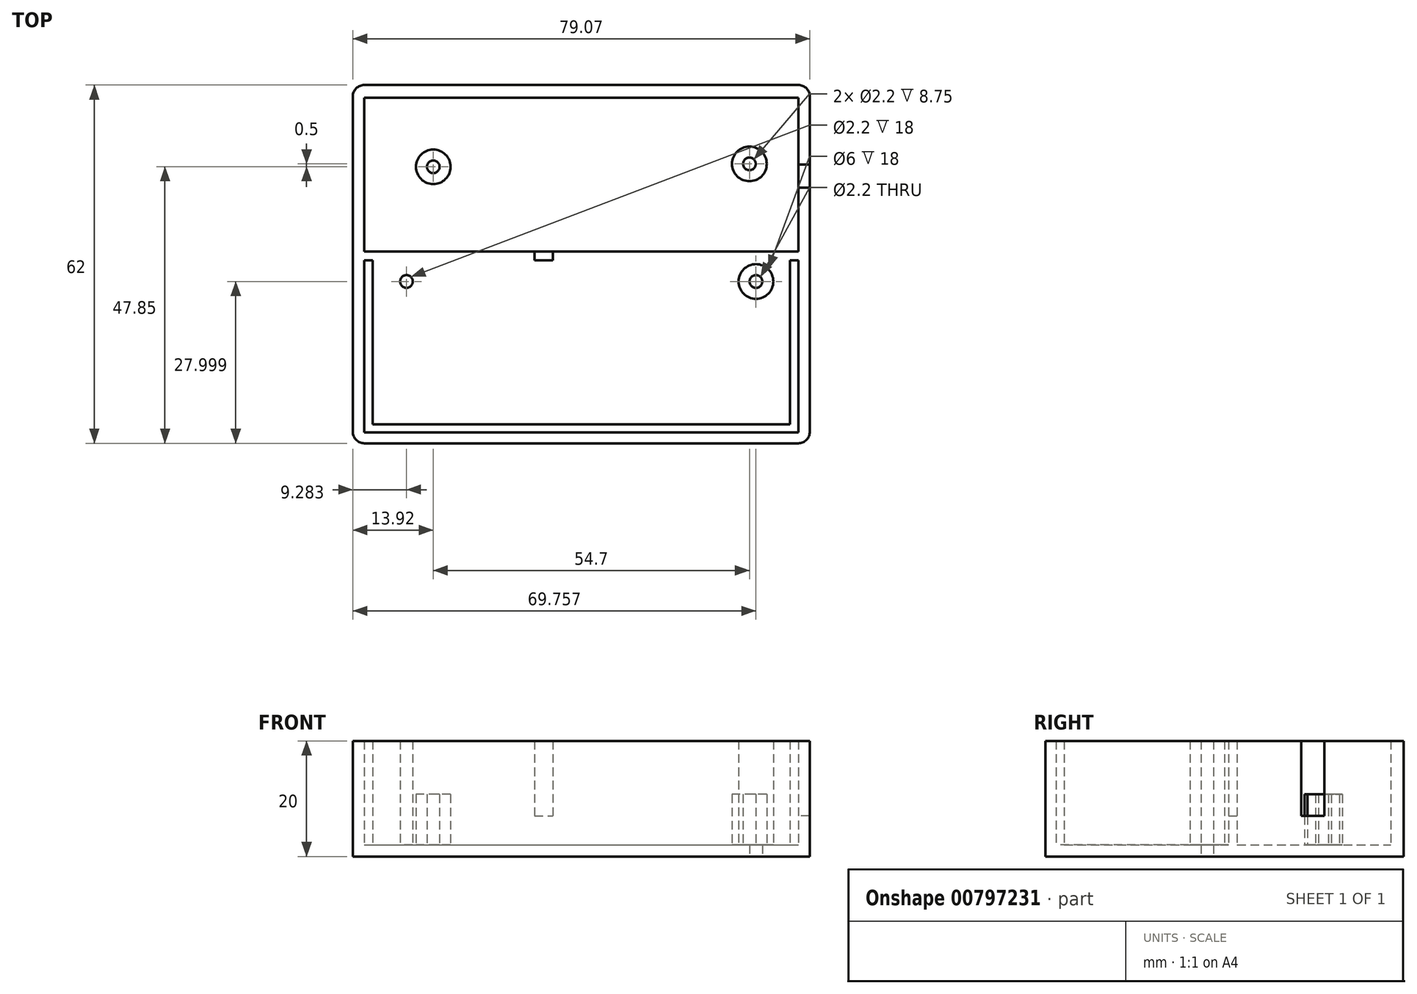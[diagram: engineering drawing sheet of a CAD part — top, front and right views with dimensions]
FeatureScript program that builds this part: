
annotation { "Feature Type Name" : "Feature", "Feature Type Description" : "" }
export const myFeature = defineFeature(function(context is Context, id is Id, definition is map)
    precondition{}
    {
        {
            var Q0;
            Q0=qCreatedBy(makeId("Top.planeOp"),FACE);
            var sketch = newSketch(context, id + "F0", { "sketchPlane" : qUnion([Q0])});
            skPoint(sketch, "E0.middle", {"position": v(0, 0) * mm});
            skLineSegment(sketch, "E1.bottom", {"start": v(36.1, -12.1) * mm, "end": v(-36.1, -12.1) * mm});
            skLineSegment(sketch, "E1.top", {"start": v(36.1, 12.1) * mm, "end": v(-36.1, 12.1) * mm});
            skLineSegment(sketch, "E1.left", {"start": v(36.1, -12.1) * mm, "end": v(36.1, 12.1) * mm});
            skLineSegment(sketch, "E1.right", {"start": v(-36.1, -12.1) * mm, "end": v(-36.1, 12.1) * mm});
            skLineSegment(sketch, "E2", {"start": v(-36.1, 12.1) * mm, "end": v(-25.6, 12.1) * mm});
            skLineSegment(sketch, "E3", {"start": v(-25.6, 12.1) * mm, "end": v(-25.6, 1.6) * mm});
            skLineSegment(sketch, "E4", {"start": v(36.1, 12.1) * mm, "end": v(29.1, 12.1) * mm});
            skLineSegment(sketch, "E5", {"start": v(29.1, 12.1) * mm, "end": v(29.1, 2.1) * mm});
            skLineSegment(sketch, "E6", {"start": v(-37.55, -12.1) * mm, "end": v(-37.55, 13.53) * mm});
            skLineSegment(sketch, "E7", {"start": v(37.55, -2) * mm, "end": v(37.55, 13.53) * mm});
            skLineSegment(sketch, "E8.bottom", {"start": v(-39.55, 15.75) * mm, "end": v(39.55, 15.75) * mm});
            skCircle(sketch, "E9", {"center": v(-25.6, 1.6) * mm, "radius": 3 * mm});
            skCircle(sketch, "E10", {"center": v(29.1, 2.1) * mm, "radius": 3 * mm});
            skCircle(sketch, "E11", {"center": v(-25.6, 1.6) * mm, "radius": 1.1 * mm});
            skCircle(sketch, "E12", {"center": v(29.1, 2.1) * mm, "radius": 1.1 * mm});
            skLineSegment(sketch, "E13", {"start": v(-25.6, 1.6) * mm, "end": v(-22.6, 1.6) * mm});
            skLineSegment(sketch, "E14", {"start": v(39.55, 0) * mm, "end": v(39.55, -2) * mm});
            skLineSegment(sketch, "E15", {"start": v(39.55, 0) * mm, "end": v(39.55, 2) * mm});
            skLineSegment(sketch, "E16", {"start": v(39.55, 2) * mm, "end": v(37.55, 2) * mm});
            skLineSegment(sketch, "E17", {"start": v(39.55, -2) * mm, "end": v(37.55, -2) * mm});
            skLineSegment(sketch, "E18", {"start": v(-36.1, -14.56) * mm, "end": v(36.1, -14.56) * mm});
            skLineSegment(sketch, "E19", {"start": v(-37.55, 13.53) * mm, "end": v(37.55, 13.53) * mm});
            skLineSegment(sketch, "E20", {"start": v(36.1, -43) * mm, "end": v(36.1, -14.56) * mm});
            skLineSegment(sketch, "E21.bottom", {"start": v(39.55, 15.75) * mm, "end": v(-39.52, 15.75) * mm});
            skLineSegment(sketch, "E21.left", {"start": v(39.55, 15.75) * mm, "end": v(39.55, -46.25) * mm});
            skLineSegment(sketch, "E21.right", {"start": v(-39.52, 15.75) * mm, "end": v(-39.52, -46.25) * mm});
            skLineSegment(sketch, "E22.top", {"start": v(-37.55, -44.4) * mm, "end": v(37.55, -44.4) * mm});
            skLineSegment(sketch, "E22.left", {"start": v(-37.55, 13.53) * mm, "end": v(-37.55, -12.1) * mm});
            skLineSegment(sketch, "E22.right", {"start": v(37.55, 13.53) * mm, "end": v(37.55, -2) * mm});
            skLineSegment(sketch, "E23.bottom", {"start": v(-36.1, 12.1) * mm, "end": v(36.1, 12.1) * mm});
            skLineSegment(sketch, "E23.top", {"start": v(-36.1, -43) * mm, "end": v(36.1, -43) * mm});
            skLineSegment(sketch, "E23.left", {"start": v(-36.1, 12.1) * mm, "end": v(-36.1, -12.1) * mm});
            skLineSegment(sketch, "E23.right", {"start": v(36.1, 12.1) * mm, "end": v(36.1, -12.1) * mm});
            skLineSegment(sketch, "E24", {"start": v(-39.52, -46.25) * mm, "end": v(39.55, -46.25) * mm});
            skLineSegment(sketch, "E25", {"start": v(36.1, -14.56) * mm, "end": v(37.55, -14.56) * mm});
            skLineSegment(sketch, "E26", {"start": v(-36.1, -14.56) * mm, "end": v(-37.55, -14.56) * mm});
            skLineSegment(sketch, "E27.trimOffspring", {"start": v(-36.1, -14.56) * mm, "end": v(-36.1, -43) * mm});
            skLineSegment(sketch, "E28.trimOffspring", {"start": v(-37.55, -14.56) * mm, "end": v(-37.55, -44.4) * mm});
            skLineSegment(sketch, "E29.trimOffspring", {"start": v(36.1, -14.56) * mm, "end": v(36.1, -43) * mm});
            skLineSegment(sketch, "E30.trimOffspring", {"start": v(37.55, -14.56) * mm, "end": v(37.55, -44.4) * mm});
            skLineSegment(sketch, "E31", {"start": v(-8.1, -13.07) * mm, "end": v(-8.1, -14.56) * mm});
            skLineSegment(sketch, "E32", {"start": v(-4.93, -14.56) * mm, "end": v(-4.93, -13.07) * mm});
            skCircle(sketch, "E33", {"center": v(-30.24, -18.25) * mm, "radius": 1.1 * mm});
            skCircle(sketch, "E34", {"center": v(-30.24, -18.25) * mm, "radius": 3 * mm});
            skLineSegment(sketch, "E35", {"start": v(0, 0) * mm, "end": v(0, 7.6) * mm});
            skCircle(sketch, "E36.MirrorC", {"center": v(30.24, -18.25) * mm, "radius": 3 * mm});
            skCircle(sketch, "E37.MirrorC", {"center": v(30.24, -18.25) * mm, "radius": 1.1 * mm});
            skLineSegment(sketch, "E38", {"start": v(-37.55, 13.53) * mm, "end": v(-37.55, -13.07) * mm});
            skLineSegment(sketch, "E39", {"start": v(-37.55, -13.07) * mm, "end": v(37.55, -13.07) * mm});
            skLineSegment(sketch, "E40", {"start": v(37.55, -13.07) * mm, "end": v(37.55, -2) * mm});
            skSolve(sketch);
        }
        {
            var Q0;
            {var subQ10=sQuery(id+"F0.wireOp",EDGE,"E16");Q0=makeQuery(id+"F0.imprint","IMPRINT",FACE,{"disambiguationData":[TD([[makeQuery(id+"F0.imprint","IMPRINT",EDGE,{"derivedFrom":subQ10}),-1.0]])]});}
            var Q1;
            Q1=makeQuery(id+"F0.imprint","IMPRINT",FACE,{"disambiguationData":[TD([[makeQuery(id+"F0.imprint","IMPRINT",EDGE,{"derivedFrom":sQuery(id+"F0.wireOp",EDGE,"E33")}),-1.0]])]});
            var Q2;
            Q2=makeQuery(id+"F0.imprint","IMPRINT",FACE,{"disambiguationData":[TD([[makeQuery(id+"F0.imprint","IMPRINT",EDGE,{"derivedFrom":sQuery(id+"F0.wireOp",EDGE,"E36.MirrorC")}),-1.0]])]});
            extrude(context, id + "F1", {"entities" : qUnion([Q0, Q1, Q2]), "depth" : 20 * mm, "offsetDistance" : 25 * mm});
        }
        {
            var Q0;
            {var subQ1=sQuery(id+"F0.wireOp",EDGE,"10jvvfjq-hym9-82hP-UYhz-ddacBWfpMkSF.top");Q0=makeQuery(id+"F0.imprint","IMPRINT",FACE,{"disambiguationData":[TD([[makeQuery(id+"F0.imprint","IMPRINT",EDGE,{"derivedFrom":subQ1}),1.0]])]});}
            var Q1;
            {var subQ0=sQuery(id+"F0.wireOp",EDGE,"E1.right");Q1=makeQuery(id+"F0.imprint","IMPRINT",FACE,{"disambiguationData":[TD([[makeQuery(id+"F0.imprint","IMPRINT",EDGE,{"derivedFrom":subQ0}),1.0]])]});}
            var Q2;
            {var subQ0=sQuery(id+"F0.wireOp",EDGE,"10jvvfjq-hym9-82hP-UYhz-ddacBWfpMkSF.bottom");Q2=makeQuery(id+"F0.imprint","IMPRINT",FACE,{"disambiguationData":[TD([[makeQuery(id+"F0.imprint","IMPRINT",EDGE,{"derivedFrom":subQ0}),-1.0]])]});}
            var Q3;
            {var subQ0=sQuery(id+"F0.wireOp",EDGE,"E1.left");Q3=makeQuery(id+"F0.imprint","IMPRINT",FACE,{"disambiguationData":[TD([[makeQuery(id+"F0.imprint","IMPRINT",EDGE,{"derivedFrom":subQ0}),-1.0]])]});}
            var Q4;
            {var subQ8=sQuery(id+"F0.wireOp",EDGE,"E1.top");Q4=makeQuery(id+"F0.imprint","IMPRINT",FACE,{"disambiguationData":[TD([[makeQuery(id+"F0.imprint","IMPRINT",EDGE,{"derivedFrom":subQ8}),1.0]])]});}
            var Q5;
            {var subQ0=sQuery(id+"F0.wireOp",EDGE,"E13");var subQ1=sQuery(id+"F0.wireOp",EDGE,"E3");var subQ2=makeQuery(id+"F0.imprint","INTERSECT",VERTEX,{"derivedFrom":[subQ1,subQ0]});Q5=makeQuery(id+"F0.imprint","IMPRINT",FACE,{"disambiguationData":[TD([[makeQuery(id+"F0.imprint","IMPRINT",EDGE,{"disambiguationData":[TD([[subQ2,1.0]])],"derivedFrom":subQ1}),-1.0]])]});}
            var Q6;
            {var subQ0=sQuery(id+"F0.wireOp",EDGE,"E13");var subQ1=sQuery(id+"F0.wireOp",EDGE,"E3");var subQ2=makeQuery(id+"F0.imprint","INTERSECT",VERTEX,{"derivedFrom":[subQ1,subQ0]});Q6=makeQuery(id+"F0.imprint","IMPRINT",FACE,{"disambiguationData":[TD([[makeQuery(id+"F0.imprint","IMPRINT",EDGE,{"disambiguationData":[TD([[subQ2,1.0]])],"derivedFrom":subQ1}),1.0]])]});}
            var Q7;
            Q7=makeQuery(id+"F0.imprint","IMPRINT",FACE,{"disambiguationData":[TD([[makeQuery(id+"F0.imprint","IMPRINT",EDGE,{"derivedFrom":sQuery(id+"F0.wireOp",EDGE,"E12")}),1.0]])]});
            var Q8;
            {var subQ7=sQuery(id+"F0.wireOp",EDGE,"E1.bottom");Q8=makeQuery(id+"F0.imprint","IMPRINT",FACE,{"disambiguationData":[TD([[makeQuery(id+"F0.imprint","IMPRINT",EDGE,{"derivedFrom":subQ7}),-1.0]])]});}
            var Q9;
            {var subQ0=sQuery(id+"F0.wireOp",EDGE,"E18");Q9=makeQuery(id+"F0.imprint","IMPRINT",FACE,{"disambiguationData":[TD([[makeQuery(id+"F0.imprint","IMPRINT",EDGE,{"derivedFrom":subQ0}),-1.0]])]});}
            var Q10;
            {var subQ10=sQuery(id+"F0.wireOp",EDGE,"E19");Q10=makeQuery(id+"F0.imprint","IMPRINT",FACE,{"disambiguationData":[TD([[makeQuery(id+"F0.imprint","IMPRINT",EDGE,{"derivedFrom":subQ10}),-1.0]])]});}
            var Q11;
            Q11=makeQuery(id+"F0.imprint","IMPRINT",FACE,{"disambiguationData":[TD([[makeQuery(id+"F0.imprint","IMPRINT",EDGE,{"derivedFrom":sQuery(id+"F0.wireOp",EDGE,"E22.top")}),1.0]])]});
            var Q12;
            Q12=makeQuery(id+"F0.imprint","IMPRINT",FACE,{"disambiguationData":[TD([[makeQuery(id+"F0.imprint","IMPRINT",EDGE,{"derivedFrom":sQuery(id+"F0.wireOp",EDGE,"E33")}),1.0]])]});
            var Q13;
            Q13=makeQuery(id+"F0.imprint","IMPRINT",FACE,{"disambiguationData":[TD([[makeQuery(id+"F0.imprint","IMPRINT",EDGE,{"derivedFrom":sQuery(id+"F0.wireOp",EDGE,"E37.MirrorC")}),-1.0]])]});
            extrude(context, id + "F2", {"entities" : qUnion([Q0, Q1, Q2, Q3, Q4, Q5, Q6, Q7, Q8, Q9, Q10, Q11, Q12, Q13]), "operationType" : NewBodyOperationType.ADD, "depth" : 2 * mm, "offsetDistance" : 25 * mm});
        }
        {
            var Q0;
            {var subQ0=sQuery(id+"F0.wireOp",EDGE,"E9");var subQ1=sQuery(id+"F0.wireOp",EDGE,"E3");var subQ2=makeQuery(id+"F0.imprint","INTERSECT",VERTEX,{"derivedFrom":[subQ1,subQ0]});Q0=makeQuery(id+"F0.imprint","IMPRINT",FACE,{"disambiguationData":[TD([[makeQuery(id+"F0.imprint","IMPRINT",EDGE,{"disambiguationData":[TD([[subQ2,-1.0]])],"derivedFrom":subQ1}),-1.0]])]});}
            var Q1;
            {var subQ0=sQuery(id+"F0.wireOp",EDGE,"E9");var subQ1=sQuery(id+"F0.wireOp",EDGE,"E3");var subQ2=makeQuery(id+"F0.imprint","INTERSECT",VERTEX,{"derivedFrom":[subQ1,subQ0]});Q1=makeQuery(id+"F0.imprint","IMPRINT",FACE,{"disambiguationData":[TD([[makeQuery(id+"F0.imprint","IMPRINT",EDGE,{"disambiguationData":[TD([[subQ2,-1.0]])],"derivedFrom":subQ1}),1.0]])]});}
            var Q2;
            Q2=makeQuery(id+"F0.imprint","IMPRINT",FACE,{"disambiguationData":[TD([[makeQuery(id+"F0.imprint","IMPRINT",EDGE,{"derivedFrom":sQuery(id+"F0.wireOp",EDGE,"E10")}),1.0]])]});
            extrude(context, id + "F3", {"entities" : qUnion([Q0, Q1, Q2]), "operationType" : NewBodyOperationType.ADD, "depth" : 10.75 * mm, "offsetDistance" : 25 * mm});
        }
        {
            var Q0;
            Q0=makeQuery(id+"F0.imprint","IMPRINT",FACE,{"disambiguationData":[TD([[makeQuery(id+"F0.imprint","IMPRINT",EDGE,{"derivedFrom":sQuery(id+"F0.wireOp",EDGE,"E14")}),-1.0]])]});
            var Q1;
            {var subQ0=sQuery(id+"F0.wireOp",EDGE,"E16");Q1=makeQuery(id+"F0.imprint","IMPRINT",FACE,{"disambiguationData":[TD([[makeQuery(id+"F0.imprint","IMPRINT",EDGE,{"derivedFrom":subQ0}),1.0]])]});}
            var Q2;
            {var subQ0=sQuery(id+"F0.wireOp",EDGE,"E31");Q2=makeQuery(id+"F0.imprint","IMPRINT",FACE,{"disambiguationData":[TD([[makeQuery(id+"F0.imprint","IMPRINT",EDGE,{"derivedFrom":subQ0}),1.0]])]});}
            extrude(context, id + "F4", {"entities" : qUnion([Q0, Q1, Q2]), "operationType" : NewBodyOperationType.ADD, "depth" : 7 * mm, "offsetDistance" : 25 * mm});
        }
        {
            var Q0;
            Q0=makeQuery(id+"F1.opExtrude","SWEPT_EDGE",EDGE,{"disambiguationData":[OSD([sQuery(id+"F0.wireOp",EDGE,"E21.left"),sQuery(id+"F0.wireOp",EDGE,"E24")])]});
            var Q1;
            Q1=makeQuery(id+"F1.opExtrude","SWEPT_EDGE",EDGE,{"disambiguationData":[OSD([sQuery(id+"F0.wireOp",EDGE,"E21.bottom"),sQuery(id+"F0.wireOp",EDGE,"E21.left")])]});
            var Q2;
            Q2=makeQuery(id+"F1.opExtrude","SWEPT_EDGE",EDGE,{"disambiguationData":[OSD([sQuery(id+"F0.wireOp",EDGE,"E21.bottom"),sQuery(id+"F0.wireOp",EDGE,"E21.right")])]});
            var Q3;
            Q3=makeQuery(id+"F1.opExtrude","SWEPT_EDGE",EDGE,{"disambiguationData":[OSD([sQuery(id+"F0.wireOp",EDGE,"E21.right"),sQuery(id+"F0.wireOp",EDGE,"E24")])]});
            fillet(context, id + "F5", {"entities" : qUnion([Q0, Q1, Q2, Q3]), "radius" : 2 * mm, "tangentPropagation" : true, "allowEdgeOverflow" : false});
        }
    });
